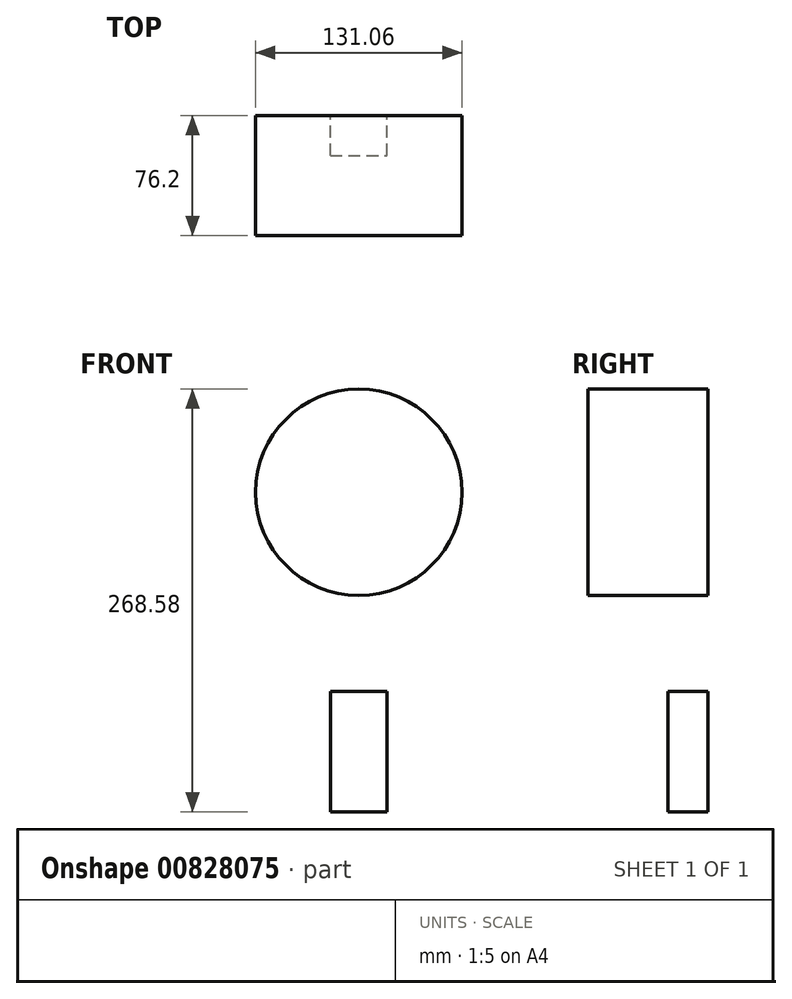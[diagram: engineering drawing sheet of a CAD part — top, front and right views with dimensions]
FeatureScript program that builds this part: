
annotation { "Feature Type Name" : "Feature", "Feature Type Description" : "" }
export const myFeature = defineFeature(function(context is Context, id is Id, definition is map)
    precondition{}
    {
        {
            var Q0;
            Q0=qCreatedBy(makeId("Front.planeOp"),FACE);
            var sketch = newSketch(context, id + "F0", { "sketchPlane" : qUnion([Q0])});
            skCircle(sketch, "E0", {"center": v(0, 0) * mm, "radius": 65.53 * mm});
            skSolve(sketch);
        }
        {
            var Q0;
            Q0=makeQuery(id+"F0.imprint","IMPRINT",FACE,{"disambiguationData":[TD([[makeQuery(id+"F0.imprint","IMPRINT",EDGE,{"derivedFrom":sQuery(id+"F0.wireOp",EDGE,"E0")}),1.0]])]});
            extrude(context, id + "F1", {"entities" : qUnion([Q0]), "depth" : 76.2 * mm, "offsetDistance" : 25.4 * mm});
        }
        {
            var Q0;
            Q0=qCreatedBy(makeId("Front.planeOp"),FACE);
            var sketch = newSketch(context, id + "F2", { "sketchPlane" : qUnion([Q0])});
            skLineSegment(sketch, "E1.bottom", {"start": v(-18.06, -203.05) * mm, "end": v(18.06, -203.05) * mm});
            skLineSegment(sketch, "E1.top", {"start": v(-18.06, -126.5) * mm, "end": v(18.06, -126.5) * mm});
            skLineSegment(sketch, "E1.left", {"start": v(-18.06, -203.05) * mm, "end": v(-18.06, -126.5) * mm});
            skLineSegment(sketch, "E1.right", {"start": v(18.06, -203.05) * mm, "end": v(18.06, -126.5) * mm});
            skPoint(sketch, "E1.middle", {"position": v(0, -164.77) * mm});
            skSolve(sketch);
        }
        {
            var Q0;
            Q0=makeQuery(id+"F2.imprint","IMPRINT",FACE,{"disambiguationData":[TD([[makeQuery(id+"F2.imprint","IMPRINT",EDGE,{"derivedFrom":sQuery(id+"F2.wireOp",EDGE,"E1.bottom")}),1.0]])]});
            extrude(context, id + "F3", {"entities" : qUnion([Q0]), "depth" : 25.4 * mm, "offsetDistance" : 25.4 * mm});
        }
    });
